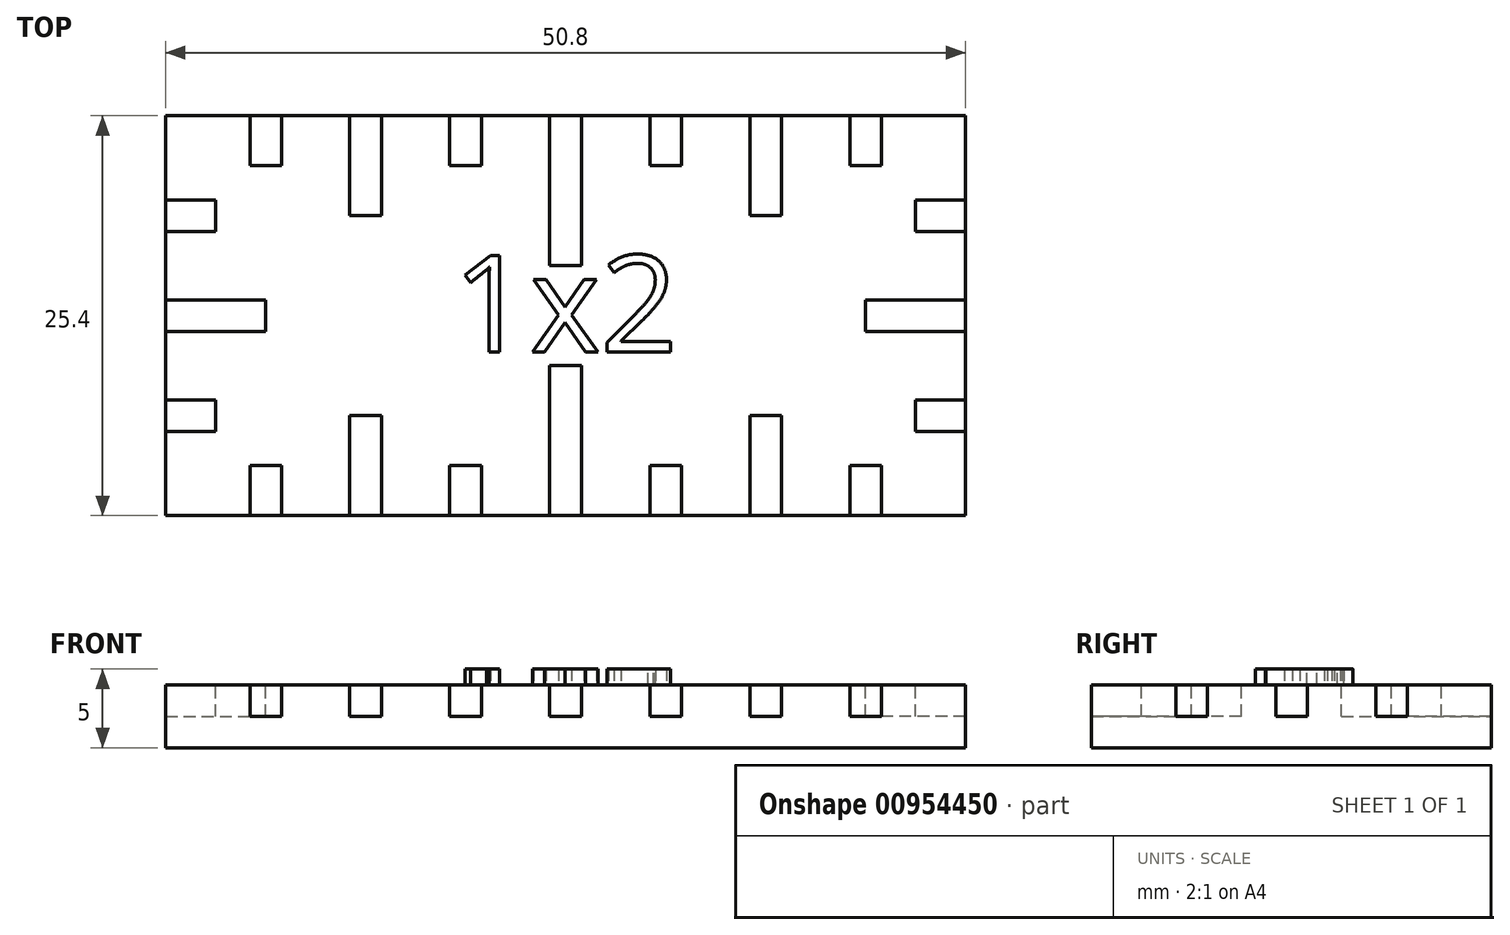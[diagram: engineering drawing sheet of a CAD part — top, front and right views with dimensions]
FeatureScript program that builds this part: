
annotation { "Feature Type Name" : "Feature", "Feature Type Description" : "" }
export const myFeature = defineFeature(function(context is Context, id is Id, definition is map)
    precondition{}
    {
        {
            var Q0;
            Q0=qCreatedBy(makeId("Top.planeOp"),FACE);
            var sketch = newSketch(context, id + "F0", { "sketchPlane" : qUnion([Q0])});
            skLineSegment(sketch, "E0.bottom", {"start": v(-25.4, 12.7) * mm, "end": v(25.4, 12.7) * mm});
            skLineSegment(sketch, "E0.top", {"start": v(-25.4, -12.7) * mm, "end": v(25.4, -12.7) * mm});
            skLineSegment(sketch, "E0.left", {"start": v(-25.4, 12.7) * mm, "end": v(-25.4, -12.7) * mm});
            skLineSegment(sketch, "E0.right", {"start": v(25.4, 12.7) * mm, "end": v(25.4, -12.7) * mm});
            skPoint(sketch, "E0.middle", {"position": v(0, 0) * mm});
            skSolve(sketch);
        }
        {
            var Q0;
            Q0=makeQuery(id+"F0.imprint","IMPRINT",FACE,{"disambiguationData":[TD([[makeQuery(id+"F0.imprint","IMPRINT",EDGE,{"derivedFrom":sQuery(id+"F0.wireOp",EDGE,"E0.bottom")}),-1.0]])]});
            extrude(context, id + "F1", {"entities" : qUnion([Q0]), "depth" : 4 * mm, "offsetDistance" : 25 * mm});
        }
        {
            var Q0;
            Q0=makeQuery(id+"F1.opExtrude","CAP_FACE",FACE,{"disambiguationData":[OSD([sQuery(id+"F0.wireOp",EDGE,"E0.bottom"),sQuery(id+"F0.wireOp",EDGE,"E0.top"),sQuery(id+"F0.wireOp",EDGE,"E0.left"),sQuery(id+"F0.wireOp",EDGE,"E0.right")])],"isStart":false});
            var sketch = newSketch(context, id + "F2", { "sketchPlane" : qUnion([Q0])});
            skLineSegment(sketch, "E1.bottom", {"start": v(-1, -3.17) * mm, "end": v(1, -3.17) * mm});
            skLineSegment(sketch, "E1.top", {"start": v(-1, -22.23) * mm, "end": v(1, -22.23) * mm});
            skLineSegment(sketch, "E1.left", {"start": v(-1, -3.17) * mm, "end": v(-1, -22.23) * mm});
            skLineSegment(sketch, "E1.right", {"start": v(1, -3.17) * mm, "end": v(1, -22.23) * mm});
            skPoint(sketch, "E1.middle", {"position": v(0, -12.7) * mm});
            skLineSegment(sketch, "E2.bottom", {"start": v(5.35, -9.53) * mm, "end": v(7.35, -9.53) * mm});
            skLineSegment(sketch, "E2.top", {"start": v(5.35, -15.88) * mm, "end": v(7.35, -15.88) * mm});
            skLineSegment(sketch, "E2.left", {"start": v(5.35, -9.53) * mm, "end": v(5.35, -15.88) * mm});
            skLineSegment(sketch, "E2.right", {"start": v(7.35, -9.53) * mm, "end": v(7.35, -15.88) * mm});
            skPoint(sketch, "E2.middle", {"position": v(6.35, -12.7) * mm});
            skLineSegment(sketch, "E3.bottom", {"start": v(-7.35, -9.53) * mm, "end": v(-5.35, -9.53) * mm});
            skLineSegment(sketch, "E3.top", {"start": v(-7.35, -15.88) * mm, "end": v(-5.35, -15.88) * mm});
            skLineSegment(sketch, "E3.left", {"start": v(-7.35, -9.53) * mm, "end": v(-7.35, -15.88) * mm});
            skLineSegment(sketch, "E3.right", {"start": v(-5.35, -9.53) * mm, "end": v(-5.35, -15.88) * mm});
            skPoint(sketch, "E3.middle", {"position": v(-6.35, -12.7) * mm});
            skLineSegment(sketch, "E4.bottom", {"start": v(-31.75, -1) * mm, "end": v(-31.75, 1) * mm});
            skLineSegment(sketch, "E4.top", {"start": v(-19.05, -1) * mm, "end": v(-19.05, 1) * mm});
            skLineSegment(sketch, "E4.left", {"start": v(-31.75, -1) * mm, "end": v(-19.05, -1) * mm});
            skLineSegment(sketch, "E4.right", {"start": v(-31.75, 1) * mm, "end": v(-19.05, 1) * mm});
            skPoint(sketch, "E4.middle", {"position": v(-25.4, 0) * mm});
            skLineSegment(sketch, "E5.bottom", {"start": v(-28.58, 5.35) * mm, "end": v(-28.58, 7.35) * mm});
            skLineSegment(sketch, "E5.top", {"start": v(-22.23, 5.35) * mm, "end": v(-22.23, 7.35) * mm});
            skLineSegment(sketch, "E5.left", {"start": v(-28.58, 5.35) * mm, "end": v(-22.23, 5.35) * mm});
            skLineSegment(sketch, "E5.right", {"start": v(-28.58, 7.35) * mm, "end": v(-22.23, 7.35) * mm});
            skPoint(sketch, "E5.middle", {"position": v(-25.4, 6.35) * mm});
            skLineSegment(sketch, "E6.bottom", {"start": v(-28.58, -7.35) * mm, "end": v(-28.58, -5.35) * mm});
            skLineSegment(sketch, "E6.top", {"start": v(-22.23, -7.35) * mm, "end": v(-22.23, -5.35) * mm});
            skLineSegment(sketch, "E6.left", {"start": v(-28.58, -7.35) * mm, "end": v(-22.23, -7.35) * mm});
            skLineSegment(sketch, "E6.right", {"start": v(-28.58, -5.35) * mm, "end": v(-22.23, -5.35) * mm});
            skPoint(sketch, "E6.middle", {"position": v(-25.4, -6.35) * mm});
            skLineSegment(sketch, "E7.bottom", {"start": v(1, 3.17) * mm, "end": v(-1, 3.17) * mm});
            skLineSegment(sketch, "E7.top", {"start": v(1, 22.22) * mm, "end": v(-1, 22.22) * mm});
            skLineSegment(sketch, "E7.left", {"start": v(1, 3.17) * mm, "end": v(1, 22.22) * mm});
            skLineSegment(sketch, "E7.right", {"start": v(-1, 3.17) * mm, "end": v(-1, 22.22) * mm});
            skPoint(sketch, "E7.middle", {"position": v(0, 12.7) * mm});
            skLineSegment(sketch, "E8.bottom", {"start": v(-5.35, 9.53) * mm, "end": v(-7.35, 9.53) * mm});
            skLineSegment(sketch, "E8.top", {"start": v(-5.35, 15.88) * mm, "end": v(-7.35, 15.88) * mm});
            skLineSegment(sketch, "E8.left", {"start": v(-5.35, 9.53) * mm, "end": v(-5.35, 15.88) * mm});
            skLineSegment(sketch, "E8.right", {"start": v(-7.35, 9.53) * mm, "end": v(-7.35, 15.88) * mm});
            skPoint(sketch, "E8.middle", {"position": v(-6.35, 12.7) * mm});
            skLineSegment(sketch, "E9.bottom", {"start": v(7.35, 9.52) * mm, "end": v(5.35, 9.52) * mm});
            skLineSegment(sketch, "E9.top", {"start": v(7.35, 15.88) * mm, "end": v(5.35, 15.88) * mm});
            skLineSegment(sketch, "E9.left", {"start": v(7.35, 9.52) * mm, "end": v(7.35, 15.88) * mm});
            skLineSegment(sketch, "E9.right", {"start": v(5.35, 9.52) * mm, "end": v(5.35, 15.88) * mm});
            skPoint(sketch, "E9.middle", {"position": v(6.35, 12.7) * mm});
            skLineSegment(sketch, "E10.bottom", {"start": v(31.75, 1) * mm, "end": v(31.75, -1) * mm});
            skLineSegment(sketch, "E10.top", {"start": v(19.05, 1) * mm, "end": v(19.05, -1) * mm});
            skLineSegment(sketch, "E10.left", {"start": v(31.75, 1) * mm, "end": v(19.05, 1) * mm});
            skLineSegment(sketch, "E10.right", {"start": v(31.75, -1) * mm, "end": v(19.05, -1) * mm});
            skPoint(sketch, "E10.middle", {"position": v(25.4, 0) * mm});
            skLineSegment(sketch, "E11.bottom", {"start": v(28.57, -5.35) * mm, "end": v(28.57, -7.35) * mm});
            skLineSegment(sketch, "E11.top", {"start": v(22.22, -5.35) * mm, "end": v(22.22, -7.35) * mm});
            skLineSegment(sketch, "E11.left", {"start": v(28.57, -5.35) * mm, "end": v(22.22, -5.35) * mm});
            skLineSegment(sketch, "E11.right", {"start": v(28.57, -7.35) * mm, "end": v(22.22, -7.35) * mm});
            skPoint(sketch, "E11.middle", {"position": v(25.4, -6.35) * mm});
            skLineSegment(sketch, "E12.bottom", {"start": v(28.58, 7.35) * mm, "end": v(28.58, 5.35) * mm});
            skLineSegment(sketch, "E12.top", {"start": v(22.23, 7.35) * mm, "end": v(22.23, 5.35) * mm});
            skLineSegment(sketch, "E12.left", {"start": v(28.57, 7.35) * mm, "end": v(22.23, 7.35) * mm});
            skLineSegment(sketch, "E12.right", {"start": v(28.58, 5.35) * mm, "end": v(22.23, 5.35) * mm});
            skPoint(sketch, "E12.middle", {"position": v(25.4, 6.35) * mm});
            skLineSegment(sketch, "E13.bottom", {"start": v(-11.7, 6.35) * mm, "end": v(-13.7, 6.35) * mm});
            skLineSegment(sketch, "E13.top", {"start": v(-11.7, 19.05) * mm, "end": v(-13.7, 19.05) * mm});
            skLineSegment(sketch, "E13.left", {"start": v(-11.7, 6.35) * mm, "end": v(-11.7, 19.05) * mm});
            skLineSegment(sketch, "E13.right", {"start": v(-13.7, 6.35) * mm, "end": v(-13.7, 19.05) * mm});
            skPoint(sketch, "E13.middle", {"position": v(-12.7, 12.7) * mm});
            skLineSegment(sketch, "E14.bottom", {"start": v(-18.05, 9.53) * mm, "end": v(-20.05, 9.53) * mm});
            skLineSegment(sketch, "E14.top", {"start": v(-18.05, 15.88) * mm, "end": v(-20.05, 15.88) * mm});
            skLineSegment(sketch, "E14.left", {"start": v(-18.05, 9.53) * mm, "end": v(-18.05, 15.88) * mm});
            skLineSegment(sketch, "E14.right", {"start": v(-20.05, 9.53) * mm, "end": v(-20.05, 15.88) * mm});
            skPoint(sketch, "E14.middle", {"position": v(-19.05, 12.7) * mm});
            skLineSegment(sketch, "E15.bottom", {"start": v(-11.7, -19.05) * mm, "end": v(-13.7, -19.05) * mm});
            skLineSegment(sketch, "E15.top", {"start": v(-11.7, -6.35) * mm, "end": v(-13.7, -6.35) * mm});
            skLineSegment(sketch, "E15.left", {"start": v(-11.7, -19.05) * mm, "end": v(-11.7, -6.35) * mm});
            skLineSegment(sketch, "E15.right", {"start": v(-13.7, -19.05) * mm, "end": v(-13.7, -6.35) * mm});
            skPoint(sketch, "E15.middle", {"position": v(-12.7, -12.7) * mm});
            skLineSegment(sketch, "E16.bottom", {"start": v(-18.05, -15.88) * mm, "end": v(-20.05, -15.88) * mm});
            skLineSegment(sketch, "E16.top", {"start": v(-18.05, -9.53) * mm, "end": v(-20.05, -9.53) * mm});
            skLineSegment(sketch, "E16.left", {"start": v(-18.05, -15.88) * mm, "end": v(-18.05, -9.53) * mm});
            skLineSegment(sketch, "E16.right", {"start": v(-20.05, -15.88) * mm, "end": v(-20.05, -9.53) * mm});
            skPoint(sketch, "E16.middle", {"position": v(-19.05, -12.7) * mm});
            skLineSegment(sketch, "E17.bottom", {"start": v(-5.35, -15.88) * mm, "end": v(-7.35, -15.88) * mm});
            skLineSegment(sketch, "E17.top", {"start": v(-5.35, -9.53) * mm, "end": v(-7.35, -9.53) * mm});
            skLineSegment(sketch, "E17.left", {"start": v(-5.35, -15.88) * mm, "end": v(-5.35, -9.53) * mm});
            skLineSegment(sketch, "E17.right", {"start": v(-7.35, -15.88) * mm, "end": v(-7.35, -9.53) * mm});
            skLineSegment(sketch, "E18.bottom", {"start": v(11.7, -6.35) * mm, "end": v(13.7, -6.35) * mm});
            skLineSegment(sketch, "E18.top", {"start": v(11.7, -19.05) * mm, "end": v(13.7, -19.05) * mm});
            skLineSegment(sketch, "E18.left", {"start": v(11.7, -6.35) * mm, "end": v(11.7, -19.05) * mm});
            skLineSegment(sketch, "E18.right", {"start": v(13.7, -6.35) * mm, "end": v(13.7, -19.05) * mm});
            skPoint(sketch, "E18.middle", {"position": v(12.7, -12.7) * mm});
            skLineSegment(sketch, "E19.bottom", {"start": v(18.05, -9.53) * mm, "end": v(20.05, -9.53) * mm});
            skLineSegment(sketch, "E19.top", {"start": v(18.05, -15.88) * mm, "end": v(20.05, -15.88) * mm});
            skLineSegment(sketch, "E19.left", {"start": v(18.05, -9.53) * mm, "end": v(18.05, -15.88) * mm});
            skLineSegment(sketch, "E19.right", {"start": v(20.05, -9.53) * mm, "end": v(20.05, -15.88) * mm});
            skPoint(sketch, "E19.middle", {"position": v(19.05, -12.7) * mm});
            skLineSegment(sketch, "E20.bottom", {"start": v(11.7, 19.05) * mm, "end": v(13.7, 19.05) * mm});
            skLineSegment(sketch, "E20.top", {"start": v(11.7, 6.35) * mm, "end": v(13.7, 6.35) * mm});
            skLineSegment(sketch, "E20.left", {"start": v(11.7, 19.05) * mm, "end": v(11.7, 6.35) * mm});
            skLineSegment(sketch, "E20.right", {"start": v(13.7, 19.05) * mm, "end": v(13.7, 6.35) * mm});
            skPoint(sketch, "E20.middle", {"position": v(12.7, 12.7) * mm});
            skLineSegment(sketch, "E21.bottom", {"start": v(18.05, 15.88) * mm, "end": v(20.05, 15.88) * mm});
            skLineSegment(sketch, "E21.top", {"start": v(18.05, 9.53) * mm, "end": v(20.05, 9.53) * mm});
            skLineSegment(sketch, "E21.left", {"start": v(18.05, 15.88) * mm, "end": v(18.05, 9.53) * mm});
            skLineSegment(sketch, "E21.right", {"start": v(20.05, 15.88) * mm, "end": v(20.05, 9.53) * mm});
            skPoint(sketch, "E21.middle", {"position": v(19.05, 12.7) * mm});
            skLineSegment(sketch, "E22.bottom", {"start": v(5.35, 15.88) * mm, "end": v(7.35, 15.88) * mm});
            skLineSegment(sketch, "E22.top", {"start": v(5.35, 9.53) * mm, "end": v(7.35, 9.53) * mm});
            skLineSegment(sketch, "E22.left", {"start": v(5.35, 15.88) * mm, "end": v(5.35, 9.53) * mm});
            skLineSegment(sketch, "E22.right", {"start": v(7.35, 15.88) * mm, "end": v(7.35, 9.53) * mm});
            skSolve(sketch);
        }
        {
            var Q0;
            Q0=qSketchRegion(id+"F2",true);
            extrude(context, id + "F3", {"entities" : qUnion([Q0]), "operationType" : NewBodyOperationType.REMOVE, "oppositeDirection" : true, "depth" : 2 * mm, "offsetDistance" : 25 * mm});
        }
        {
            var Q0;
            Q0=makeQuery(id+"F1.opExtrude","CAP_FACE",FACE,{"disambiguationData":[OSD([sQuery(id+"F0.wireOp",EDGE,"E0.bottom"),sQuery(id+"F0.wireOp",EDGE,"E0.top"),sQuery(id+"F0.wireOp",EDGE,"E0.left"),sQuery(id+"F0.wireOp",EDGE,"E0.right")])],"isStart":false});
            var sketch = newSketch(context, id + "F4", { "sketchPlane" : qUnion([Q0])});
            skText(sketch, "E23", { "text": "1x2", "fontName": "OpenSans-Regular.ttf"});
            const initialGuessF4  = {"E23": [-0.00718, -0.0023, 1, 0, 0.00618]};
            skSetInitialGuess(sketch, initialGuessF4);
            skSolve(sketch);
        }
        {
            var Q0;
            Q0 = qSketchRegion(id + "F4", true);
            extrude(context, id + "F5", {"entities" : qUnion([Q0]), "depth" : 1 * mm, "offsetDistance" : 25 * mm});
        }
    });
